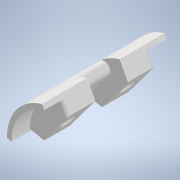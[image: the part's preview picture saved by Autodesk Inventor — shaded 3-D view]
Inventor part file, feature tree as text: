
AUTODESK INVENTOR PART (.ipt)
format: ipt  version: 2022 (Build 260153000, 153)  size: 206,336 bytes
history: native  units: mm
features: reference x6, other x5, extrude x5, sketch x5, fillet x3, projected_geometry x2
ambient origin geometry x8: Origin, YZ Plane, XZ Plane, XY Plane, X Axis, Y Axis, Z Axis, Center Point
bodies: Body1 (feature_tree)
feature tree (26):
  other  "Твердое тело1"
  extrude  "Выдавливание1"  Depth=0.2mm
  extrude  "Выдавливание2"  Depth=0.2mm
  extrude  "Выдавливание3"  Depth=34.0mm TaperAngle=0.0deg
  extrude  "Выдавливание5"  Depth=24.0mm TaperAngle=0.0deg
  extrude  "Выдавливание6"  Depth=4.0mm
  fillet  "Сопряжение2"  Radius=15.0mm
  fillet  "Сопряжение3"  Radius=4.0mm
  fillet  "Сопряжение4"  Radius=9.0mm
  sketch  "Эскиз1"
  reference  "Ссылка1"
  reference  "Ссылка2"
  sketch  "Эскиз2"
  reference  "Ссылка3"
  reference  "Ссылка4"
  sketch  "Эскиз3"
  projected_geometry  "Спроецированная петля1"
  reference  "Ссылка5"
  sketch  "Эскиз5"
  reference  "Ссылка6"
  sketch  "Эскиз6"
  projected_geometry  "Спроецированная петля3"
  other  "<userpath>\Documents\Git\MZCAT_2024\MZCAT.iam"
  other  "MZCAT.iam"
  other  "base:1"
  other  "CAT_protector:1"
